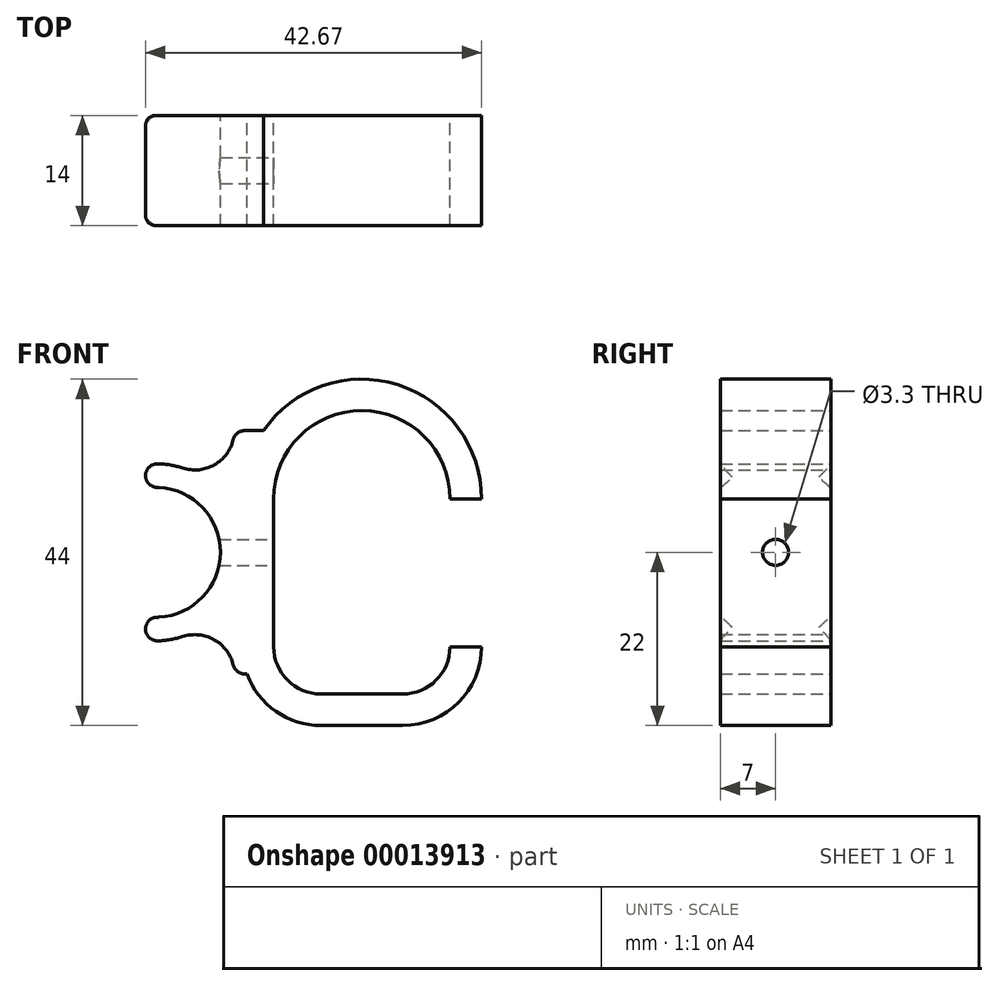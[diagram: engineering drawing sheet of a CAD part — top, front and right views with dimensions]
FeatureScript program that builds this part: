
annotation { "Feature Type Name" : "Feature", "Feature Type Description" : "" }
export const myFeature = defineFeature(function(context is Context, id is Id, definition is map)
    precondition{}
    {
        {
            var Q0;
            Q0=qCreatedBy(makeId("Front.planeOp"),FACE);
            var sketch = newSketch(context, id + "F0", { "sketchPlane" : qUnion([Q0])});
            skArc(sketch, "E0", {"start": v(-1.08, -8.18) * mm, "mid": v(8.25, 0) * mm, "end": v(-1.08, 8.18) * mm});
            skArc(sketch, "E1", {"start": v(3.46, 10.7) * mm, "mid": v(1.02, 11.2) * mm, "end": v(-1.47, 11.15) * mm});
            skLineSegment(sketch, "E2", {"start": v(-1.08, 8.18) * mm, "end": v(-1.47, 11.15) * mm});
            skLineSegment(sketch, "E3", {"start": v(-1.08, -8.18) * mm, "end": v(-1.47, -11.15) * mm});
            skLineSegment(sketch, "E4", {"start": v(0, 0) * mm, "end": v(-11.25, 0) * mm, "construction": true});
            skLineSegment(sketch, "E5", {"start": v(10, 15.46) * mm, "end": v(10, 15.46) * mm});
            skLineSegment(sketch, "E6", {"start": v(15, 0) * mm, "end": v(15, 15.46) * mm});
            skPoint(sketch, "E7.orphan", {"position": v(8.25, 0) * mm});
            skArc(sketch, "E8.trimOffspring", {"start": v(-1.47, -11.15) * mm, "mid": v(1.02, -11.2) * mm, "end": v(3.46, -10.7) * mm});
            skArc(sketch, "E9.filletArc", {"start": v(3.46, 10.7) * mm, "mid": v(7.94, 11.42) * mm, "end": v(10, 15.46) * mm});
            skLineSegment(sketch, "E10.MirrorCS", {"start": v(15, 0) * mm, "end": v(15, -15.46) * mm});
            skLineSegment(sketch, "E11", {"start": v(10, 15.46) * mm, "end": v(15, 15.46) * mm});
            skLineSegment(sketch, "E12.MirrorCS", {"start": v(10, -15.46) * mm, "end": v(15, -15.46) * mm});
            skArc(sketch, "E13.MirrorCS", {"start": v(3.46, -10.7) * mm, "mid": v(7.94, -11.42) * mm, "end": v(10, -15.46) * mm});
            skSolve(sketch);
        }
        {
            var Q0;
            Q0=qSketchRegion(id+"F0",true);
            extrude(context, id + "F1", {"entities" : qUnion([Q0]), "depth" : 7 * mm, "hasSecondDirection" : true, "secondDirectionOppositeDirection" : true, "secondDirectionDepth" : 7 * mm});
        }
        {
            var Q0;
            Q0=makeQuery(id+"F1.opExtrude","SWEPT_FACE",FACE,{"disambiguationData":[OSD([sQuery(id+"F0.wireOp",EDGE,"E6"),sQuery(id+"F0.wireOp",EDGE,"E10.MirrorCS")])]});
            var sketch = newSketch(context, id + "F2", { "sketchPlane" : qUnion([Q0])});
            skCircle(sketch, "E14", {"center": v(0, 0) * mm, "radius": 4 * mm});
            skSolve(sketch);
        }
        {
            var Q0;
            Q0=qSketchRegion(id+"F2",true);
            extrude(context, id + "F3", {"entities" : qUnion([Q0]), "operationType" : NewBodyOperationType.REMOVE, "oppositeDirection" : true, "depth" : 3 * mm});
        }
        {
            var Q0;
            Q0=makeQuery(id+"F1.opExtrude","SWEPT_FACE",FACE,{"disambiguationData":[OSD([sQuery(id+"F0.wireOp",EDGE,"E3")])]});
            var Q1;
            Q1=makeQuery(id+"F1.opExtrude","SWEPT_FACE",FACE,{"disambiguationData":[OSD([sQuery(id+"F0.wireOp",EDGE,"E2")])]});
            var Q2;
            Q2=makeQuery(id+"F1.opExtrude","SWEPT_EDGE",EDGE,{"disambiguationData":[OSD([sQuery(id+"F0.wireOp",EDGE,"E9.filletArc"),sQuery(id+"F0.wireOp",EDGE,"E11")])]});
            var Q3;
            Q3=makeQuery(id+"F1.opExtrude","SWEPT_EDGE",EDGE,{"disambiguationData":[OSD([sQuery(id+"F0.wireOp",EDGE,"E12.MirrorCS"),sQuery(id+"F0.wireOp",EDGE,"E13.MirrorCS")])]});
            fillet(context, id + "F4", {"entities" : qUnion([Q0, Q1, Q2, Q3]), "radius" : 1.5 * mm, "tangentPropagation" : true, "allowEdgeOverflow" : false});
        }
        {
            var Q0;
            Q0=qCreatedBy(makeId("Front.planeOp"),FACE);
            var sketch = newSketch(context, id + "F5", { "sketchPlane" : qUnion([Q0])});
            skLineSegment(sketch, "E15.1", {"start": v(15, 6.8) * mm, "end": v(15, -12) * mm});
            skArc(sketch, "E16", {"start": v(15, 6.8) * mm, "mid": v(26.2, 18) * mm, "end": v(37.4, 6.8) * mm});
            skArc(sketch, "E17", {"start": v(15, -12) * mm, "mid": v(16.76, -16.24) * mm, "end": v(21, -18) * mm});
            skLineSegment(sketch, "E18", {"start": v(21, -18) * mm, "end": v(31.4, -18) * mm});
            skArc(sketch, "E19", {"start": v(31.4, -18) * mm, "mid": v(35.64, -16.24) * mm, "end": v(37.4, -12) * mm});
            skLineSegment(sketch, "E20", {"start": v(26.2, 18) * mm, "end": v(0, 18) * mm, "construction": true});
            skLineSegment(sketch, "E21", {"start": v(0, 0) * mm, "end": v(15, 0) * mm, "construction": true});
            skArc(sketch, "E22.0", {"start": v(11, 6.8) * mm, "mid": v(26.2, 22) * mm, "end": v(41.4, 6.8) * mm});
            skLineSegment(sketch, "E23", {"start": v(37.4, 6.8) * mm, "end": v(41.4, 6.8) * mm});
            skArc(sketch, "E24.0", {"start": v(31.4, -22) * mm, "mid": v(38.47, -19.07) * mm, "end": v(41.4, -12) * mm});
            skLineSegment(sketch, "E24.1", {"start": v(21, -22) * mm, "end": v(31.4, -22) * mm});
            skArc(sketch, "E24.2", {"start": v(11, -12) * mm, "mid": v(13.93, -19.07) * mm, "end": v(21, -22) * mm});
            skLineSegment(sketch, "E25", {"start": v(11, 6.8) * mm, "end": v(11, -12) * mm});
            skLineSegment(sketch, "E26", {"start": v(37.4, -12) * mm, "end": v(41.4, -12) * mm});
            skSolve(sketch);
        }
        {
            var Q0;
            Q0 = qSketchRegion(id + "F5", true);
            var Q1;
            Q1=makeQuery(id+"F1.opExtrude","CAP_FACE",FACE,{"disambiguationData":[OSD([sQuery(id+"F0.wireOp",EDGE,"E0"),sQuery(id+"F0.wireOp",EDGE,"E1"),sQuery(id+"F0.wireOp",EDGE,"E2"),sQuery(id+"F0.wireOp",EDGE,"E3"),sQuery(id+"F0.wireOp",EDGE,"E6"),sQuery(id+"F0.wireOp",EDGE,"E8.trimOffspring"),sQuery(id+"F0.wireOp",EDGE,"E9.filletArc"),sQuery(id+"F0.wireOp",EDGE,"E10.MirrorCS"),sQuery(id+"F0.wireOp",EDGE,"E11"),sQuery(id+"F0.wireOp",EDGE,"E12.MirrorCS"),sQuery(id+"F0.wireOp",EDGE,"E13.MirrorCS")])],"isStart":false});
            var Q2;
            Q2=makeQuery(id+"F1.opExtrude","CAP_FACE",FACE,{"disambiguationData":[OSD([sQuery(id+"F0.wireOp",EDGE,"E0"),sQuery(id+"F0.wireOp",EDGE,"E1"),sQuery(id+"F0.wireOp",EDGE,"E2"),sQuery(id+"F0.wireOp",EDGE,"E3"),sQuery(id+"F0.wireOp",EDGE,"E6"),sQuery(id+"F0.wireOp",EDGE,"E8.trimOffspring"),sQuery(id+"F0.wireOp",EDGE,"E9.filletArc"),sQuery(id+"F0.wireOp",EDGE,"E10.MirrorCS"),sQuery(id+"F0.wireOp",EDGE,"E11"),sQuery(id+"F0.wireOp",EDGE,"E12.MirrorCS"),sQuery(id+"F0.wireOp",EDGE,"E13.MirrorCS")])],"isStart":true});
            extrude(context, id + "F6", {"entities" : qUnion([Q0]), "operationType" : NewBodyOperationType.ADD, "endBound" : BoundingType.UP_TO_SURFACE, "endBoundEntityFace" : qUnion([Q1]), "depth" : 25 * mm, "hasSecondDirection" : true, "secondDirectionBound" : SecondDirectionBoundingType.UP_TO_SURFACE, "secondDirectionOppositeDirection" : true, "secondDirectionBoundEntityFace" : qUnion([Q2]), "secondDirectionDepth" : 25 * mm});
        }
        {
            var Q0;
            Q0=makeQuery(id+"F1.opExtrude","SWEPT_FACE",FACE,{"disambiguationData":[OSD([sQuery(id+"F0.wireOp",EDGE,"E6"),sQuery(id+"F0.wireOp",EDGE,"E10.MirrorCS")])]});
            var sketch = newSketch(context, id + "F7", { "sketchPlane" : qUnion([Q0])});
            skCircle(sketch, "E27", {"center": v(0, 0) * mm, "radius": 1.65 * mm});
            skSolve(sketch);
        }
        {
            var Q0;
            Q0=qSketchRegion(id+"F7",true);
            var Q1;
            Q1=makeQuery(id+"F1.opExtrude","SWEPT_FACE",FACE,{"disambiguationData":[OSD([sQuery(id+"F0.wireOp",EDGE,"E6"),sQuery(id+"F0.wireOp",EDGE,"E10.MirrorCS")])]});
            extrude(context, id + "F8", {"entities" : qUnion([Q0]), "operationType" : NewBodyOperationType.REMOVE, "endBound" : BoundingType.THROUGH_ALL, "oppositeDirection" : true, "endBoundEntityFace" : qUnion([Q1]), "depth" : 25 * mm});
        }
    });
